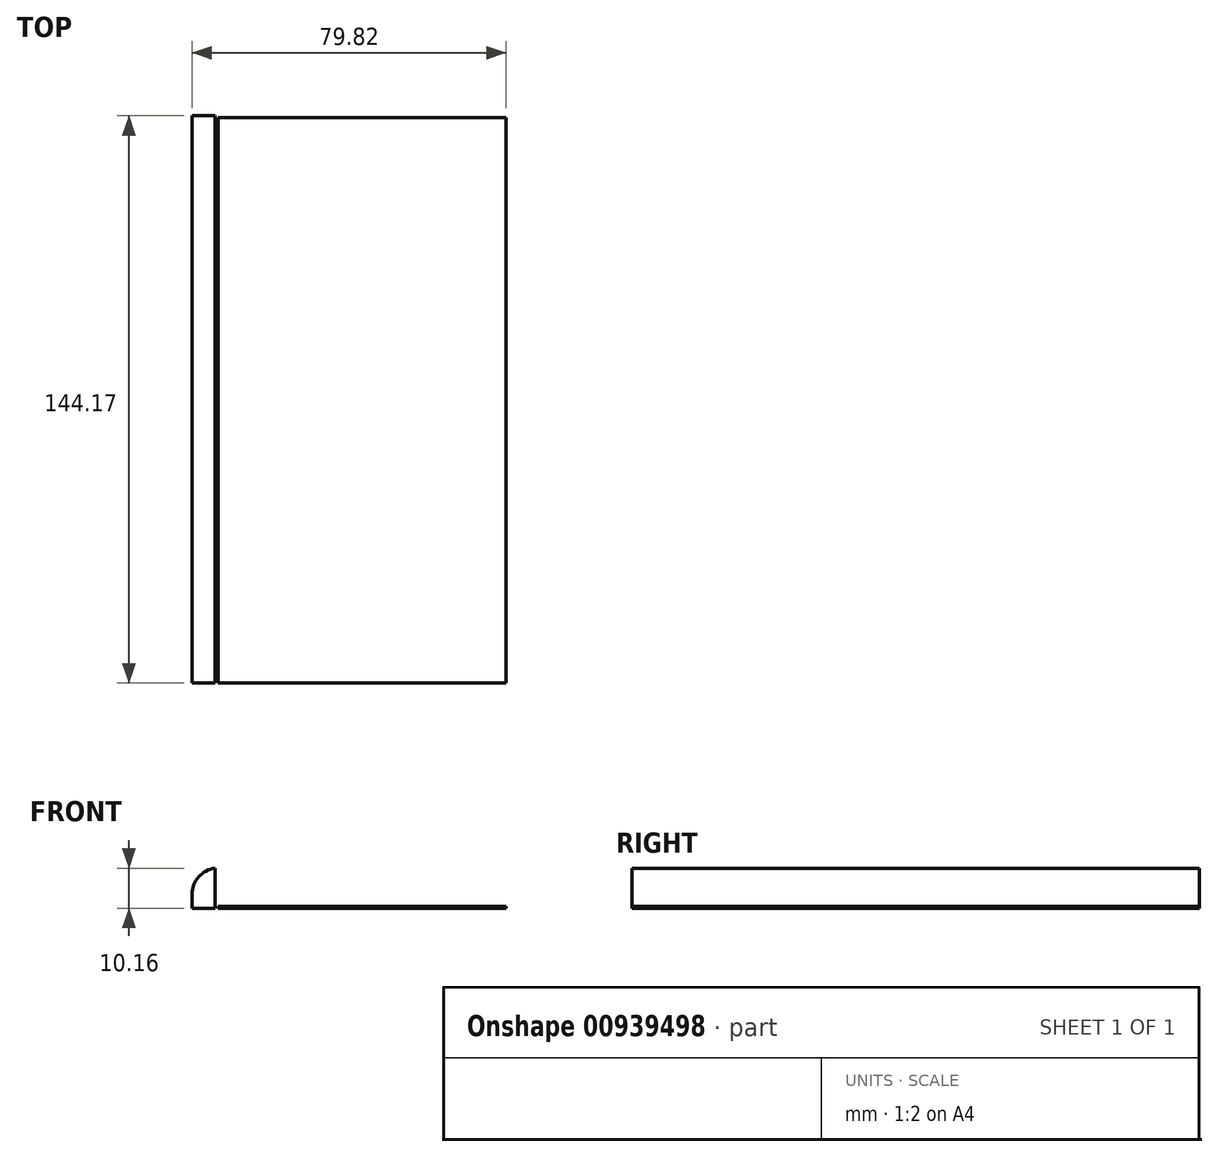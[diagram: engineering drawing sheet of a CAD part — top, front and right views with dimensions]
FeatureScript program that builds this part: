
annotation { "Feature Type Name" : "Feature", "Feature Type Description" : "" }
export const myFeature = defineFeature(function(context is Context, id is Id, definition is map)
    precondition{}
    {
        {
            var Q0;
            Q0=qCreatedBy(makeId("Top.planeOp"),FACE);
            var sketch = newSketch(context, id + "F0", { "sketchPlane" : qUnion([Q0])});
            skLineSegment(sketch, "E0.bottom", {"start": v(-54.12, 73.84) * mm, "end": v(19, 73.84) * mm});
            skLineSegment(sketch, "E0.top", {"start": v(-54.12, -69.91) * mm, "end": v(19, -69.91) * mm});
            skLineSegment(sketch, "E0.left", {"start": v(-54.12, 73.84) * mm, "end": v(-54.12, -69.91) * mm});
            skLineSegment(sketch, "E0.right", {"start": v(19, 73.84) * mm, "end": v(19, -69.91) * mm});
            skSolve(sketch);
        }
        {
            var Q0;
            Q0=qCreatedBy(makeId("Top.planeOp"),FACE);
            var sketch = newSketch(context, id + "F1", { "sketchPlane" : qUnion([Q0])});
            skLineSegment(sketch, "E1.bottom", {"start": v(-54.96, 74.26) * mm, "end": v(-60.8, 74.26) * mm});
            skLineSegment(sketch, "E1.top", {"start": v(-54.96, -69.91) * mm, "end": v(-60.8, -69.91) * mm});
            skLineSegment(sketch, "E1.left", {"start": v(-54.96, 74.26) * mm, "end": v(-54.96, -69.91) * mm});
            skLineSegment(sketch, "E1.right", {"start": v(-60.8, 74.26) * mm, "end": v(-60.8, -69.91) * mm});
            skSolve(sketch);
        }
        {
            var Q0;
            Q0=makeQuery(id+"F1.imprint","IMPRINT",FACE,{"disambiguationData":[TD([[makeQuery(id+"F1.imprint","IMPRINT",EDGE,{"derivedFrom":sQuery(id+"F1.wireOp",EDGE,"E1.bottom")}),1.0]])]});
            extrude(context, id + "F2", {"entities" : qUnion([Q0]), "depth" : 10.16 * mm, "offsetDistance" : 25.4 * mm});
        }
        {
            var Q0;
            Q0=makeQuery(id+"F0.imprint","IMPRINT",FACE,{"disambiguationData":[TD([[makeQuery(id+"F0.imprint","IMPRINT",EDGE,{"derivedFrom":sQuery(id+"F0.wireOp",EDGE,"E0.bottom")}),-1.0]])]});
            extrude(context, id + "F3", {"entities" : qUnion([Q0]), "depth" : 0.5 * mm, "offsetDistance" : 25.4 * mm});
        }
        {
            var Q0;
            Q0=makeQuery(id+"F2.opExtrude","CAP_EDGE",EDGE,{"disambiguationData":[OSD([sQuery(id+"F1.wireOp",EDGE,"E1.right")])],"isStart":false});
            fillet(context, id + "F4", {"entities" : qUnion([Q0]), "radius" : 6.75 * mm, "tangentPropagation" : true, "allowEdgeOverflow" : false});
        }
    });
